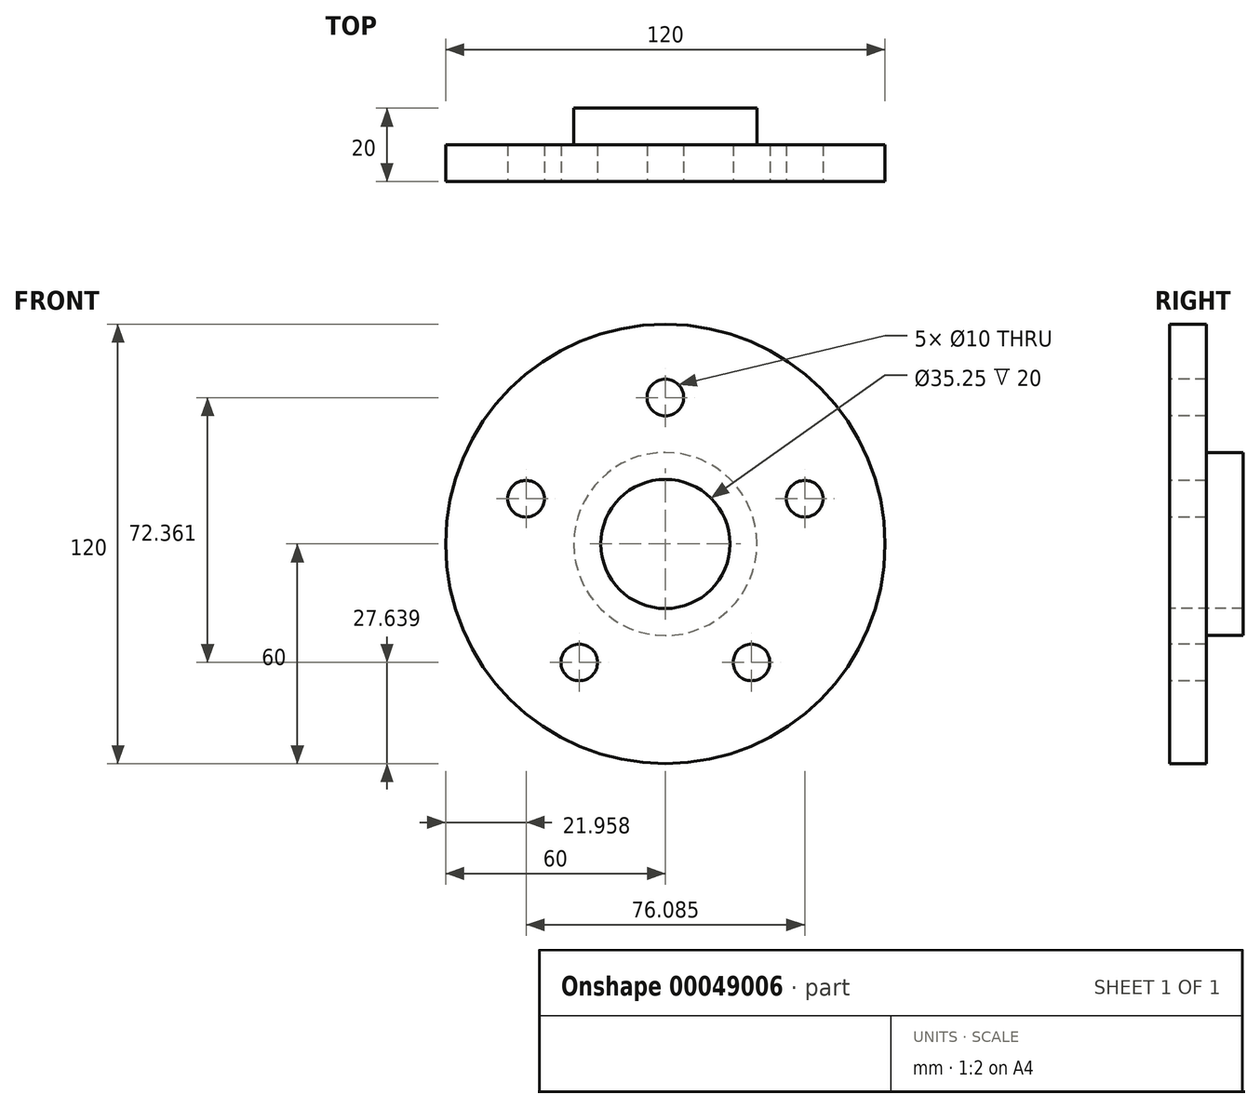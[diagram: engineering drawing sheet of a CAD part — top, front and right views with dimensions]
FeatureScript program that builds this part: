
annotation { "Feature Type Name" : "Feature", "Feature Type Description" : "" }
export const myFeature = defineFeature(function(context is Context, id is Id, definition is map)
    precondition{}
    {
        {
            var Q0;
            Q0=qCreatedBy(makeId("Front.planeOp"),FACE);
            var sketch = newSketch(context, id + "F0", { "sketchPlane" : qUnion([Q0])});
            skCircle(sketch, "E0", {"center": v(0, 0) * mm, "radius": 25 * mm});
            skSolve(sketch);
        }
        {
            var Q0;
            Q0=qSketchRegion(id+"F0",true);
            extrude(context, id + "F1", {"entities" : qUnion([Q0]), "oppositeDirection" : true, "depth" : 10 * mm});
        }
        {
            var Q0;
            Q0=qCreatedBy(makeId("Front.planeOp"),FACE);
            var sketch = newSketch(context, id + "F2", { "sketchPlane" : qUnion([Q0])});
            skCircle(sketch, "E1", {"center": v(0, 0) * mm, "radius": 60 * mm});
            skSolve(sketch);
        }
        {
            var Q0;
            Q0=makeQuery(id+"F2.imprint","IMPRINT",FACE,{"disambiguationData":[TD([[makeQuery(id+"F2.imprint","IMPRINT",EDGE,{"derivedFrom":sQuery(id+"F2.wireOp",EDGE,"E1")}),1.0]])]});
            extrude(context, id + "F3", {"entities" : qUnion([Q0]), "operationType" : NewBodyOperationType.ADD, "depth" : 10 * mm});
        }
        {
            var Q0;
            Q0=makeQuery(id+"F3.opExtrude","CAP_FACE",FACE,{"disambiguationData":[OSD([sQuery(id+"F2.wireOp",EDGE,"E1")])],"isStart":false});
            var sketch = newSketch(context, id + "F4", { "sketchPlane" : qUnion([Q0])});
            skCircle(sketch, "E2", {"center": v(0, 40) * mm, "radius": 5 * mm});
            skCircle(sketch, "E3.1.0", {"center": v(-38.04, 12.36) * mm, "radius": 5 * mm});
            skCircle(sketch, "E3.2.0", {"center": v(-23.51, -32.36) * mm, "radius": 5 * mm});
            skCircle(sketch, "E3.3.0", {"center": v(23.51, -32.36) * mm, "radius": 5 * mm});
            skCircle(sketch, "E3.4.0", {"center": v(38.04, 12.36) * mm, "radius": 5 * mm});
            skPoint(sketch, "E3.center", {"position": v(0, 0) * mm});
            skSolve(sketch);
        }
        {
            var Q0;
            Q0=qSketchRegion(id+"F4",true);
            extrude(context, id + "F5", {"entities" : qUnion([Q0]), "operationType" : NewBodyOperationType.REMOVE, "endBound" : BoundingType.THROUGH_ALL, "oppositeDirection" : true, "depth" : 25 * mm});
        }
        {
            var Q0;
            Q0=makeQuery(id+"F3.opExtrude","CAP_FACE",FACE,{"disambiguationData":[OSD([sQuery(id+"F2.wireOp",EDGE,"E1")])],"isStart":false});
            var sketch = newSketch(context, id + "F6", { "sketchPlane" : qUnion([Q0])});
            skCircle(sketch, "E4", {"center": v(0, 0) * mm, "radius": 17.62 * mm});
            skSolve(sketch);
        }
        {
            var Q0;
            Q0=qSketchRegion(id+"F6",true);
            extrude(context, id + "F7", {"entities" : qUnion([Q0]), "operationType" : NewBodyOperationType.REMOVE, "oppositeDirection" : true, "depth" : 50 * mm});
        }
    });
